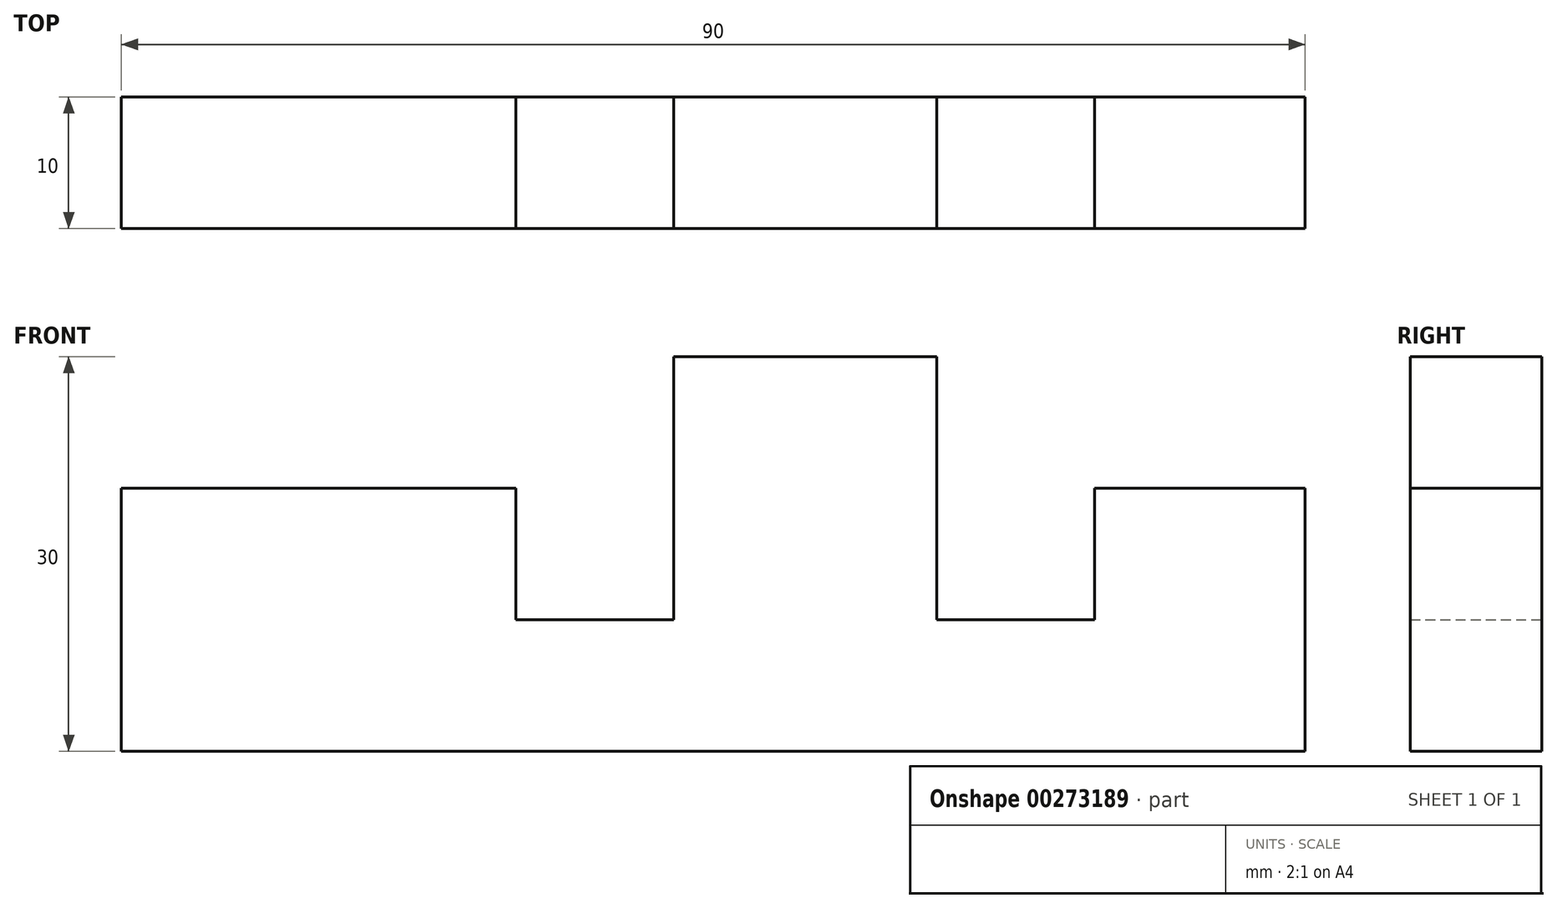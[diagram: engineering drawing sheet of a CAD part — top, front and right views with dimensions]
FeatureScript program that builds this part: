
annotation { "Feature Type Name" : "Feature", "Feature Type Description" : "" }
export const myFeature = defineFeature(function(context is Context, id is Id, definition is map)
    precondition{}
    {
        {
            var Q0;
            Q0=qCreatedBy(makeId("Front.planeOp"),FACE);
            var sketch = newSketch(context, id + "F0", { "sketchPlane" : qUnion([Q0])});
            skLineSegment(sketch, "E0", {"start": v(0, 0) * mm, "end": v(90, 0) * mm});
            skLineSegment(sketch, "E1", {"start": v(0, 0) * mm, "end": v(0, 20) * mm});
            skLineSegment(sketch, "E2", {"start": v(0, 20) * mm, "end": v(30, 20) * mm});
            skLineSegment(sketch, "E3", {"start": v(30, 20) * mm, "end": v(30, 10) * mm});
            skLineSegment(sketch, "E4", {"start": v(30, 10) * mm, "end": v(42, 10) * mm});
            skLineSegment(sketch, "E5", {"start": v(42, 10) * mm, "end": v(42, 30) * mm});
            skLineSegment(sketch, "E6", {"start": v(42, 30) * mm, "end": v(62, 30) * mm});
            skLineSegment(sketch, "E7", {"start": v(62, 30) * mm, "end": v(62, 10) * mm});
            skLineSegment(sketch, "E8", {"start": v(62, 10) * mm, "end": v(74, 10) * mm});
            skLineSegment(sketch, "E9", {"start": v(74, 10) * mm, "end": v(74, 20) * mm});
            skLineSegment(sketch, "E10", {"start": v(74, 20) * mm, "end": v(90, 20) * mm});
            skLineSegment(sketch, "E11", {"start": v(90, 20) * mm, "end": v(90, 0) * mm});
            skSolve(sketch);
        }
        {
            var Q0;
            Q0=makeQuery(id+"F0.imprint","IMPRINT",FACE,{"disambiguationData":[TD([[makeQuery(id+"F0.imprint","IMPRINT",EDGE,{"derivedFrom":sQuery(id+"F0.wireOp",EDGE,"E0")}),1.0]])]});
            extrude(context, id + "F1", {"entities" : qUnion([Q0]), "depth" : 10 * mm});
        }
    });
